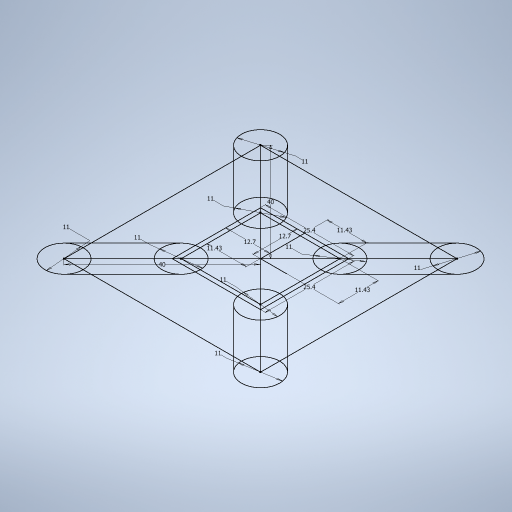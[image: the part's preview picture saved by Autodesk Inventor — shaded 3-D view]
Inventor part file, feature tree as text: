
AUTODESK INVENTOR PART (.ipt)
format: ipt  version: 2024 (Build 280153000, 153)  size: 260,096 bytes
history: native  units: in
note: dims shown in document units (in); Inventor stores cm internally (conversion verified against a paired STEP export)
features: sketch x1
ambient origin geometry x8: Origin, YZ Plane, XZ Plane, XY Plane, X Axis, Y Axis, Z Axis, Center Point
feature tree (1):
  sketch  "Sketch1"  dims[d0=1.0in d1=1.0in d2=0.5in d3=0.5in d4=1.5748in d5=1.5748in d6=0.45in d7=0.45in d8=0.45in d9=0.4331in d10=0.4331in d11=0.4331in d12=0.4331in d13=0.4331in d14=0.4331in d15=0.4331in d16=0.4331in]
